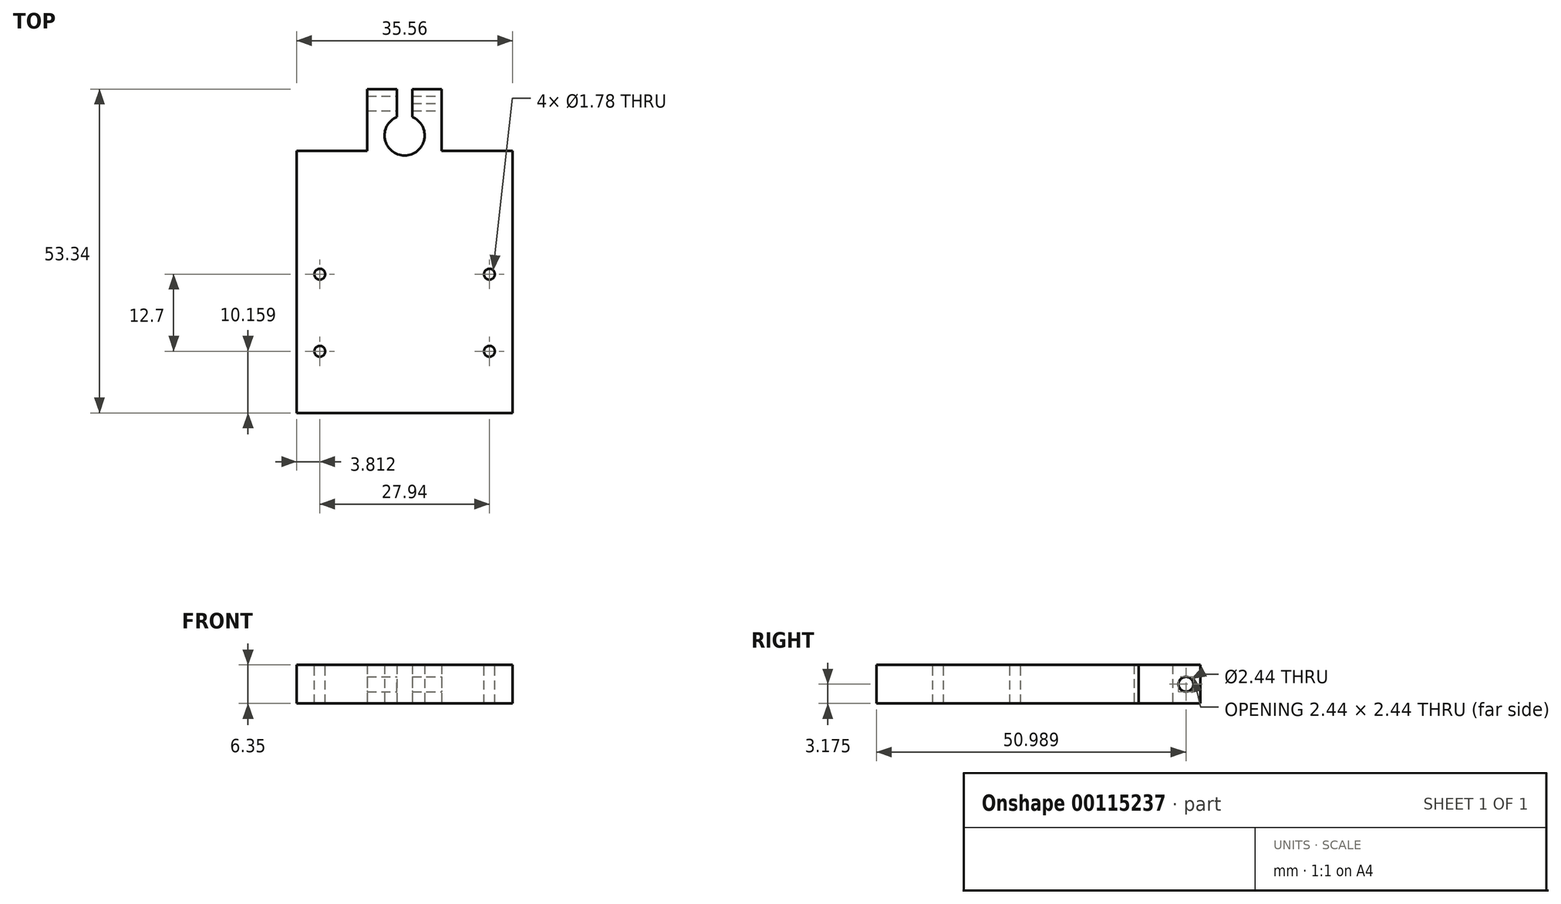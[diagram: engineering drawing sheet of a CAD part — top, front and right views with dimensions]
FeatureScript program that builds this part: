
annotation { "Feature Type Name" : "Feature", "Feature Type Description" : "" }
export const myFeature = defineFeature(function(context is Context, id is Id, definition is map)
    precondition{}
    {
        {
            var Q0;
            Q0=qCreatedBy(makeId("Top.planeOp"),FACE);
            var sketch = newSketch(context, id + "F0", { "sketchPlane" : qUnion([Q0])});
            skLineSegment(sketch, "E0.bottom", {"start": v(-11.64, 14.7) * mm, "end": v(0, 14.7) * mm});
            skLineSegment(sketch, "E0.top", {"start": v(-11.64, -28.47) * mm, "end": v(23.92, -28.47) * mm});
            skLineSegment(sketch, "E0.left", {"start": v(-11.64, 14.7) * mm, "end": v(-11.64, -28.47) * mm});
            skLineSegment(sketch, "E0.right", {"start": v(23.92, 14.7) * mm, "end": v(23.92, -28.47) * mm});
            skArc(sketch, "E1", {"start": v(4.87, 20.3) * mm, "mid": v(6.14, 13.95) * mm, "end": v(7.41, 20.3) * mm});
            skLineSegment(sketch, "E2.top", {"start": v(0, 24.87) * mm, "end": v(4.87, 24.87) * mm});
            skLineSegment(sketch, "E2.left", {"start": v(0, 14.7) * mm, "end": v(0, 24.87) * mm});
            skLineSegment(sketch, "E2.right", {"start": v(12.2, 14.7) * mm, "end": v(12.2, 24.87) * mm});
            skLineSegment(sketch, "E3", {"start": v(4.87, 24.87) * mm, "end": v(4.87, 20.3) * mm});
            skLineSegment(sketch, "E4", {"start": v(7.41, 24.87) * mm, "end": v(7.41, 20.3) * mm});
            skLineSegment(sketch, "E5.trimOffspring", {"start": v(7.41, 24.87) * mm, "end": v(12.2, 24.87) * mm});
            skLineSegment(sketch, "E6.trimOffspring", {"start": v(12.2, 14.7) * mm, "end": v(23.92, 14.7) * mm});
            skPoint(sketch, "E7.visualSharp", {"position": v(12.2, 14.7) * mm});
            skPoint(sketch, "E8.visualSharp", {"position": v(0, 14.7) * mm});
            skSolve(sketch);
        }
        {
            var Q0;
            Q0=makeQuery(id+"F0.imprint","IMPRINT",FACE,{"disambiguationData":[TD([[makeQuery(id+"F0.imprint","IMPRINT",EDGE,{"derivedFrom":sQuery(id+"F0.wireOp",EDGE,"E0.bottom")}),-1.0]])]});
            extrude(context, id + "F1", {"entities" : qUnion([Q0]), "depth" : 6.35 * mm, "offsetDistance" : 25.4 * mm});
        }
        {
            var Q0;
            Q0=makeQuery(id+"F1.opExtrude","CAP_FACE",FACE,{"disambiguationData":[OSD([sQuery(id+"F0.wireOp",EDGE,"E0.bottom"),sQuery(id+"F0.wireOp",EDGE,"E0.top"),sQuery(id+"F0.wireOp",EDGE,"E0.left"),sQuery(id+"F0.wireOp",EDGE,"E0.right"),sQuery(id+"F0.wireOp",EDGE,"E1"),sQuery(id+"F0.wireOp",EDGE,"E2.top"),sQuery(id+"F0.wireOp",EDGE,"E2.left"),sQuery(id+"F0.wireOp",EDGE,"E2.right"),sQuery(id+"F0.wireOp",EDGE,"E3"),sQuery(id+"F0.wireOp",EDGE,"E4"),sQuery(id+"F0.wireOp",EDGE,"E5.trimOffspring"),sQuery(id+"F0.wireOp",EDGE,"E6.trimOffspring")])],"isStart":false});
            var sketch = newSketch(context, id + "F2", { "sketchPlane" : qUnion([Q0])});
            skLineSegment(sketch, "E9.bottom", {"start": v(-7.83, -18.31) * mm, "end": v(20.11, -18.31) * mm});
            skLineSegment(sketch, "E9.top", {"start": v(-7.83, -5.61) * mm, "end": v(20.11, -5.61) * mm});
            skLineSegment(sketch, "E9.left", {"start": v(-7.83, -18.31) * mm, "end": v(-7.83, -5.61) * mm});
            skLineSegment(sketch, "E9.right", {"start": v(20.11, -18.31) * mm, "end": v(20.11, -5.61) * mm});
            skPoint(sketch, "E10", {"position": v(-7.83, -5.61) * mm});
            skPoint(sketch, "E11", {"position": v(20.11, -5.61) * mm});
            skPoint(sketch, "E12", {"position": v(20.11, -18.31) * mm});
            skPoint(sketch, "E13", {"position": v(-7.83, -18.31) * mm});
            skSolve(sketch);
        }
        {
            var Q0;
            Q0=sQuery(id+"F2.wireOp",VERTEX,"E10");
            var Q1;
            Q1=sQuery(id+"F2.wireOp",VERTEX,"E11");
            var Q2;
            Q2=sQuery(id+"F2.wireOp",VERTEX,"E12");
            var Q3;
            Q3=sQuery(id+"F2.wireOp",VERTEX,"E13");
            var Q4;
            Q4=makeQuery(id+"F1.opExtrude","SWEPT_BODY",BODY,{"disambiguationData":[OSD([sQuery(id+"F0.wireOp",EDGE,"E0.bottom"),sQuery(id+"F0.wireOp",EDGE,"E0.top"),sQuery(id+"F0.wireOp",EDGE,"E0.left"),sQuery(id+"F0.wireOp",EDGE,"E0.right"),sQuery(id+"F0.wireOp",EDGE,"E1"),sQuery(id+"F0.wireOp",EDGE,"E2.top"),sQuery(id+"F0.wireOp",EDGE,"E2.left"),sQuery(id+"F0.wireOp",EDGE,"E2.right"),sQuery(id+"F0.wireOp",EDGE,"E3"),sQuery(id+"F0.wireOp",EDGE,"E4"),sQuery(id+"F0.wireOp",EDGE,"E5.trimOffspring"),sQuery(id+"F0.wireOp",EDGE,"E6.trimOffspring")])]});
            hole(context, id + "F3", {"style" : HoleStyle.SIMPLE, "endStyle" : HoleEndStyle.THROUGH, "standardTappedOrClearance" : lookupTablePath({ "standard" : "ANSI", "engagement" : "75%", "pitch" : "56 tpi", "size" : "#2", "type" : "Tapped" }), "standardBlindInLast" : lookupTablePath({ "standard" : "ANSI", "engagement" : "75%", "pitch" : "56 tpi", "size" : "#2", "type" : "Tapped" }), "holeDiameter" : 1.78 * mm, "locations" : qUnion([Q0, Q1, Q2, Q3]), "scope" : qUnion([Q4]), "isTappedThrough" : true, "majorDiameter" : 2.18 * mm, "showTappedDepth" : true});
        }
        {
            var Q0;
            Q0=makeQuery(id+"F1.opExtrude","SWEPT_FACE",FACE,{"disambiguationData":[OSD([sQuery(id+"F0.wireOp",EDGE,"E2.right")])]});
            var sketch = newSketch(context, id + "F4", { "sketchPlane" : qUnion([Q0])});
            skPoint(sketch, "E14", {"position": v(22.5, 3.18) * mm});
            skSolve(sketch);
        }
        {
            var Q0;
            Q0=sQuery(id+"F4.wireOp",VERTEX,"E14");
            var Q1;
            Q1=makeQuery(id+"F1.opExtrude","SWEPT_BODY",BODY,{"disambiguationData":[OSD([sQuery(id+"F0.wireOp",EDGE,"E0.bottom"),sQuery(id+"F0.wireOp",EDGE,"E0.top"),sQuery(id+"F0.wireOp",EDGE,"E0.left"),sQuery(id+"F0.wireOp",EDGE,"E0.right"),sQuery(id+"F0.wireOp",EDGE,"E1"),sQuery(id+"F0.wireOp",EDGE,"E2.top"),sQuery(id+"F0.wireOp",EDGE,"E2.left"),sQuery(id+"F0.wireOp",EDGE,"E2.right"),sQuery(id+"F0.wireOp",EDGE,"E3"),sQuery(id+"F0.wireOp",EDGE,"E4"),sQuery(id+"F0.wireOp",EDGE,"E5.trimOffspring"),sQuery(id+"F0.wireOp",EDGE,"E6.trimOffspring"),sQuery(id+"F0.wireOp",EDGE,"b3359f59-4171-4d5f-9a57-11bbc652a131.filletArc"),sQuery(id+"F0.wireOp",EDGE,"e739ef9f-7809-4680-b41c-8175d90d6834.filletArc")])]});
            hole(context, id + "F5", {"style" : HoleStyle.SIMPLE, "endStyle" : HoleEndStyle.BLIND, "standardTappedOrClearance" : lookupTablePath({ "standard" : "ANSI", "fit" : "Normal (ASME)", "size" : "#2", "type" : "Clearance" }), "standardBlindInLast" : lookupTablePath({ "fit" : "Free", "standard" : "ANSI", "size" : "#2", "type" : "Clearance" }), "holeDiameter" : 2.44 * mm, "holeDepth" : 5.08 * mm, "locations" : qUnion([Q0]), "scope" : qUnion([Q1]), "tappedDepth" : 12.7 * mm, "tapClearance" : 3});
        }
        {
            var Q0;
            Q0=makeQuery(id+"F1.opExtrude","SWEPT_FACE",FACE,{"disambiguationData":[OSD([sQuery(id+"F0.wireOp",EDGE,"E2.right")])]});
            var sketch = newSketch(context, id + "F6", { "sketchPlane" : qUnion([Q0])});
            skPoint(sketch, "E15", {"position": v(22.52, 3.18) * mm});
            skPoint(sketch, "E15.positionSnap0", {"position": v(24.87, 3.18) * mm});
            skSolve(sketch);
        }
        {
            var Q0;
            Q0=sQuery(id+"F6.wireOp",VERTEX,"E15");
            var Q1;
            Q1=makeQuery(id+"F1.opExtrude","SWEPT_BODY",BODY,{"disambiguationData":[OSD([sQuery(id+"F0.wireOp",EDGE,"E0.bottom"),sQuery(id+"F0.wireOp",EDGE,"E0.top"),sQuery(id+"F0.wireOp",EDGE,"E0.left"),sQuery(id+"F0.wireOp",EDGE,"E0.right"),sQuery(id+"F0.wireOp",EDGE,"E1"),sQuery(id+"F0.wireOp",EDGE,"E2.top"),sQuery(id+"F0.wireOp",EDGE,"E2.left"),sQuery(id+"F0.wireOp",EDGE,"E2.right"),sQuery(id+"F0.wireOp",EDGE,"E3"),sQuery(id+"F0.wireOp",EDGE,"E4"),sQuery(id+"F0.wireOp",EDGE,"E5.trimOffspring"),sQuery(id+"F0.wireOp",EDGE,"E6.trimOffspring"),sQuery(id+"F0.wireOp",EDGE,"b3359f59-4171-4d5f-9a57-11bbc652a131.filletArc"),sQuery(id+"F0.wireOp",EDGE,"e739ef9f-7809-4680-b41c-8175d90d6834.filletArc")])]});
            hole(context, id + "F7", {"style" : HoleStyle.SIMPLE, "endStyle" : HoleEndStyle.BLIND, "standardTappedOrClearance" : lookupTablePath({ "standard" : "ANSI", "fit" : "Normal (ASME)", "size" : "#2", "type" : "Clearance" }), "standardBlindInLast" : lookupTablePath({ "fit" : "Free", "standard" : "ANSI", "size" : "#2", "type" : "Clearance" }), "holeDiameter" : 2.44 * mm, "holeDepth" : 25.4 * mm, "locations" : qUnion([Q0]), "scope" : qUnion([Q1]), "tappedDepth" : 12.7 * mm, "tapClearance" : 3});
        }
    });
